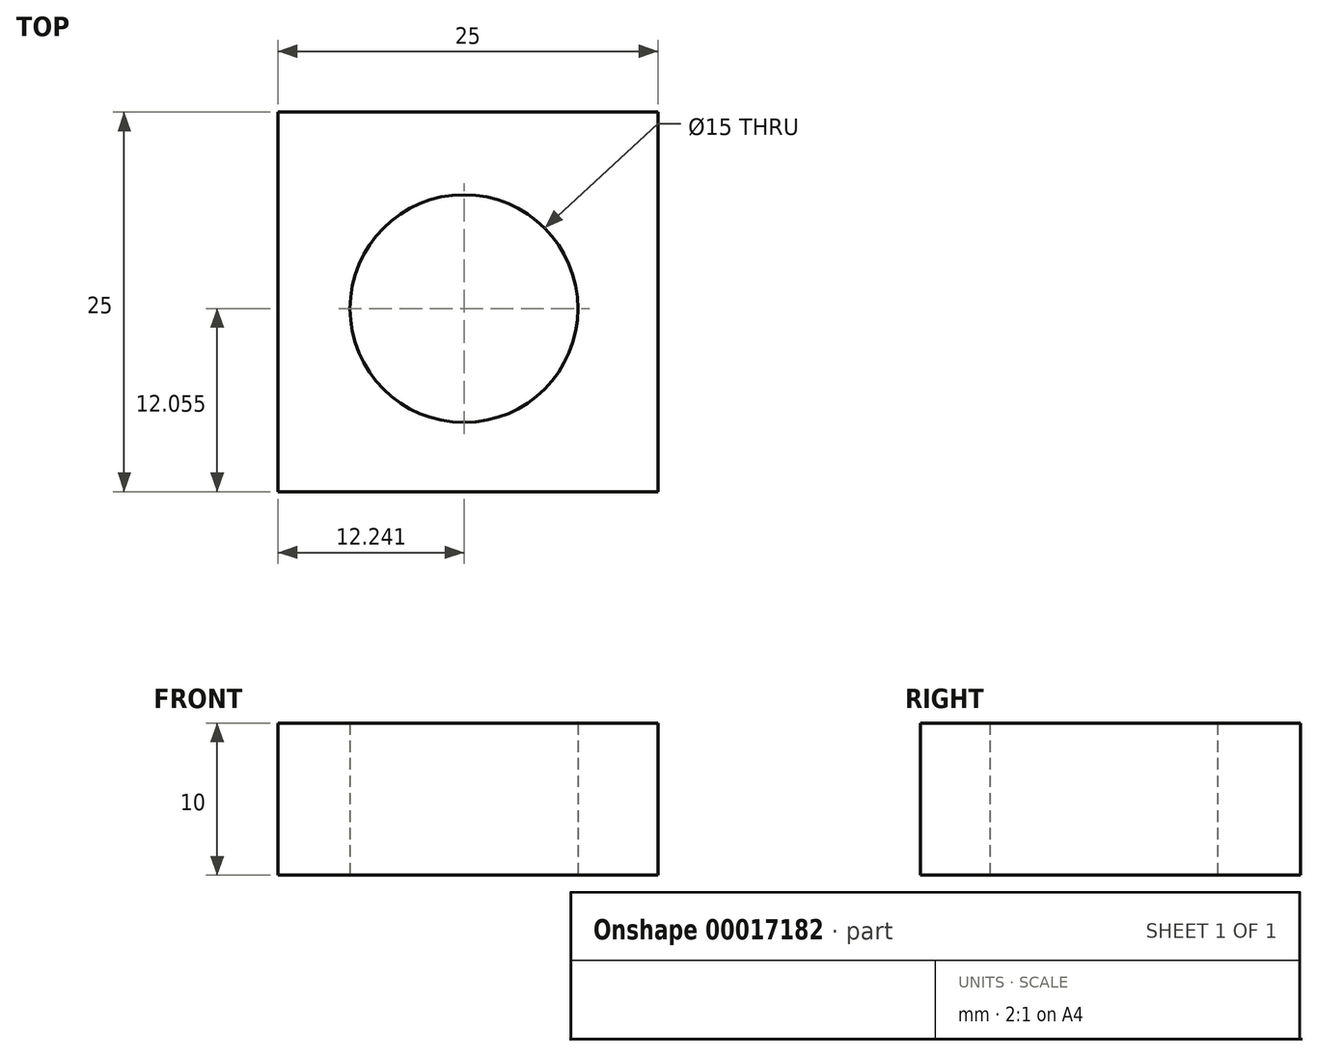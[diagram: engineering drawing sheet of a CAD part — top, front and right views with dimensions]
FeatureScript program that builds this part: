
annotation { "Feature Type Name" : "Feature", "Feature Type Description" : "" }
export const myFeature = defineFeature(function(context is Context, id is Id, definition is map)
    precondition{}
    {
        {
            var Q0;
            Q0=qCreatedBy(makeId("Top.planeOp"),FACE);
            var sketch = newSketch(context, id + "F0", { "sketchPlane" : qUnion([Q0])});
            skLineSegment(sketch, "E0.bottom", {"start": v(-9.46, 18.01) * mm, "end": v(15.54, 18.01) * mm});
            skLineSegment(sketch, "E0.top", {"start": v(-9.46, -6.99) * mm, "end": v(15.54, -6.99) * mm});
            skLineSegment(sketch, "E0.left", {"start": v(-9.46, 18.01) * mm, "end": v(-9.46, -6.99) * mm});
            skLineSegment(sketch, "E0.right", {"start": v(15.54, 18.01) * mm, "end": v(15.54, -6.99) * mm});
            skSolve(sketch);
        }
        {
            var Q0;
            Q0 = qSketchRegion(id + "F0", true);
            extrude(context, id + "F1", {"entities" : qUnion([Q0]), "depth" : 10 * mm});
        }
        {
            var Q0;
            Q0=qCreatedBy(makeId("Top.planeOp"),FACE);
            var sketch = newSketch(context, id + "F2", { "sketchPlane" : qUnion([Q0])});
            skCircle(sketch, "E1", {"center": v(2.78, 5.06) * mm, "radius": 7.5 * mm});
            skSolve(sketch);
        }
        {
            var Q0;
            Q0 = qSketchRegion(id + "F2", true);
            extrude(context, id + "F3", {"entities" : qUnion([Q0]), "operationType" : NewBodyOperationType.REMOVE, "depth" : 10 * mm});
        }
    });
